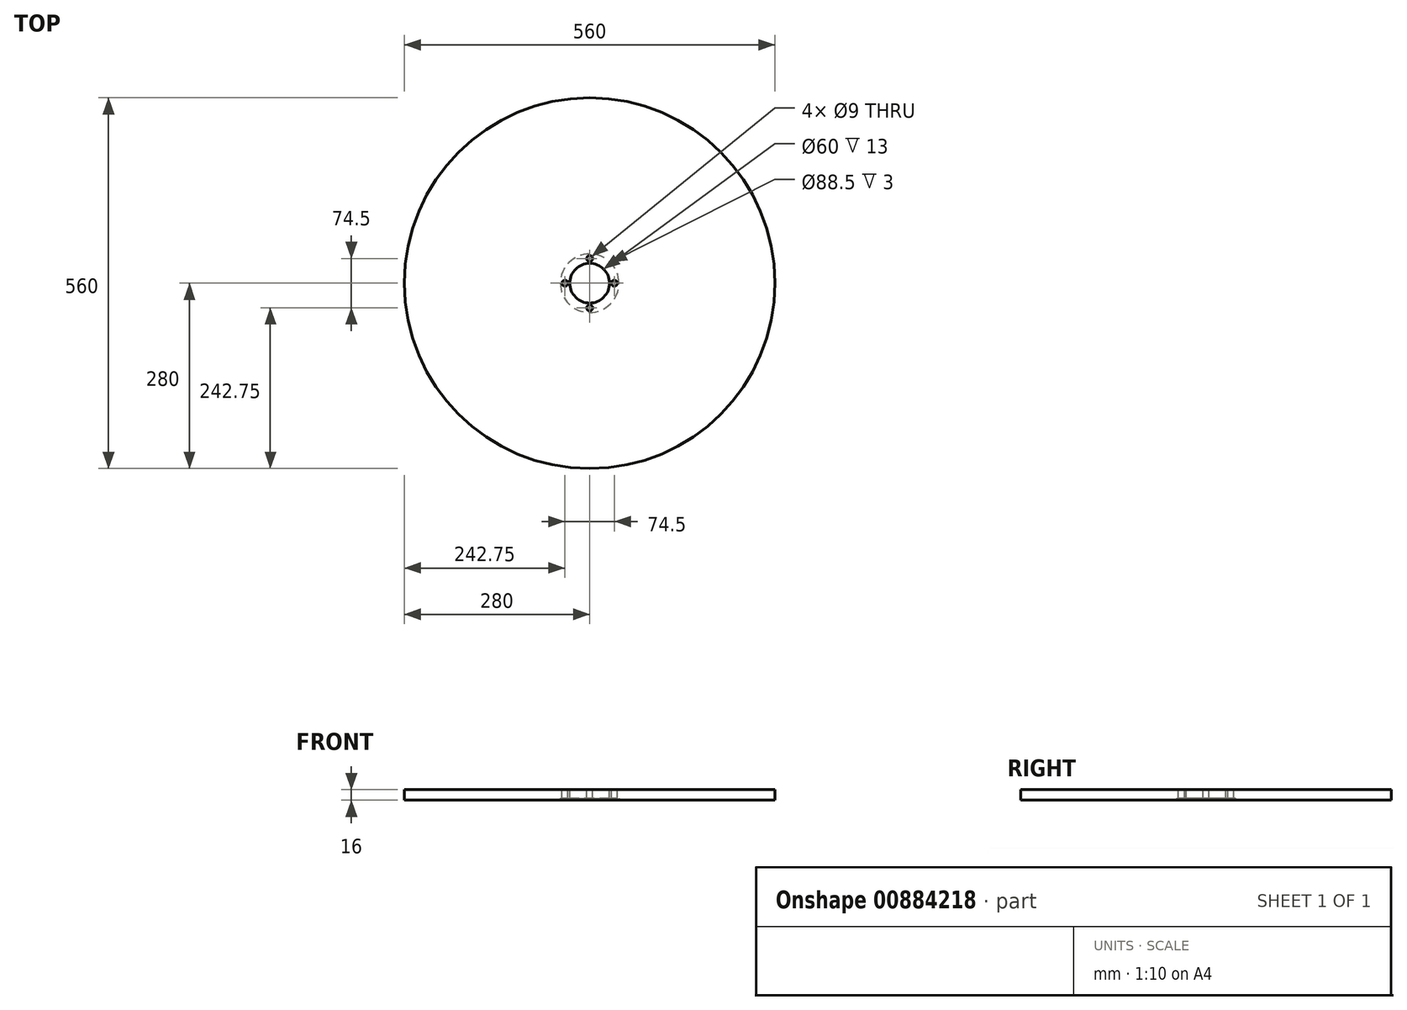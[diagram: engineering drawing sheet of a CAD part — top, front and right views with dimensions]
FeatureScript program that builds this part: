
annotation { "Feature Type Name" : "Feature", "Feature Type Description" : "" }
export const myFeature = defineFeature(function(context is Context, id is Id, definition is map)
    precondition{}
    {
        {
            var Q0;
            Q0=qCreatedBy(makeId("Top.planeOp"),FACE);
            var sketch = newSketch(context, id + "F0", { "sketchPlane" : qUnion([Q0])});
            skCircle(sketch, "E0", {"center": v(0, 0) * mm, "radius": 280 * mm});
            skSolve(sketch);
        }
        {
            var Q0;
            Q0=makeQuery(id+"F0.imprint","IMPRINT",FACE,{"disambiguationData":[TD([[makeQuery(id+"F0.imprint","IMPRINT",EDGE,{"derivedFrom":sQuery(id+"F0.wireOp",EDGE,"E0")}),1.0]])]});
            extrude(context, id + "F1", {"entities" : qUnion([Q0]), "depth" : 16 * mm, "offsetDistance" : 25 * mm});
        }
        {
            var Q0;
            Q0=makeQuery(id+"F1.opExtrude","CAP_FACE",FACE,{"disambiguationData":[OSD([sQuery(id+"F0.wireOp",EDGE,"E0")])],"isStart":false});
            var sketch = newSketch(context, id + "F2", { "sketchPlane" : qUnion([Q0])});
            skCircle(sketch, "E1", {"center": v(0, 0) * mm, "radius": 30 * mm});
            skCircle(sketch, "E2", {"center": v(0, 0) * mm, "radius": 37.25 * mm, "construction": true});
            skCircle(sketch, "E3", {"center": v(0, 37.25) * mm, "radius": 4.5 * mm});
            skCircle(sketch, "E4", {"center": v(-37.25, 0) * mm, "radius": 4.5 * mm});
            skCircle(sketch, "E5", {"center": v(37.25, 0) * mm, "radius": 4.5 * mm});
            skCircle(sketch, "E6", {"center": v(0, -37.25) * mm, "radius": 4.5 * mm});
            skSolve(sketch);
        }
        {
            var Q0;
            Q0=makeQuery(id+"F2.imprint","IMPRINT",FACE,{"disambiguationData":[TD([[makeQuery(id+"F2.imprint","IMPRINT",EDGE,{"derivedFrom":sQuery(id+"F2.wireOp",EDGE,"E1")}),1.0]])]});
            var Q1;
            Q1=makeQuery(id+"F2.imprint","IMPRINT",FACE,{"disambiguationData":[TD([[makeQuery(id+"F2.imprint","IMPRINT",EDGE,{"derivedFrom":sQuery(id+"F2.wireOp",EDGE,"HDDMHsGB-oVZA-M6vI-Bz3S-lTRq8NOSrvcb")}),1.0]])]});
            var Q2;
            Q2=makeQuery(id+"F2.imprint","IMPRINT",FACE,{"disambiguationData":[TD([[makeQuery(id+"F2.imprint","IMPRINT",EDGE,{"derivedFrom":sQuery(id+"F2.wireOp",EDGE,"E4")}),1.0]])]});
            var Q3;
            Q3=makeQuery(id+"F2.imprint","IMPRINT",FACE,{"disambiguationData":[TD([[makeQuery(id+"F2.imprint","IMPRINT",EDGE,{"derivedFrom":sQuery(id+"F2.wireOp",EDGE,"E3")}),1.0]])]});
            var Q4;
            Q4=makeQuery(id+"F2.imprint","IMPRINT",FACE,{"disambiguationData":[TD([[makeQuery(id+"F2.imprint","IMPRINT",EDGE,{"derivedFrom":sQuery(id+"F2.wireOp",EDGE,"E5")}),1.0]])]});
            var Q5;
            Q5=makeQuery(id+"F2.imprint","IMPRINT",FACE,{"disambiguationData":[TD([[makeQuery(id+"F2.imprint","IMPRINT",EDGE,{"derivedFrom":sQuery(id+"F2.wireOp",EDGE,"E6")}),1.0]])]});
            extrude(context, id + "F3", {"entities" : qUnion([Q0, Q1, Q2, Q3, Q4, Q5]), "operationType" : NewBodyOperationType.REMOVE, "oppositeDirection" : true, "depth" : 25 * mm, "offsetDistance" : 25 * mm});
        }
        {
            var Q0;
            Q0=makeQuery(id+"F1.opExtrude","CAP_FACE",FACE,{"disambiguationData":[OSD([sQuery(id+"F0.wireOp",EDGE,"E0")])],"isStart":true});
            var sketch = newSketch(context, id + "F4", { "sketchPlane" : qUnion([Q0])});
            skCircle(sketch, "E7", {"center": v(0, 0) * mm, "radius": 44.25 * mm});
            skSolve(sketch);
        }
        {
            var Q0;
            Q0=makeQuery(id+"F4.imprint","IMPRINT",FACE,{"disambiguationData":[TD([[makeQuery(id+"F4.imprint","IMPRINT",EDGE,{"derivedFrom":sQuery(id+"F4.wireOp",EDGE,"E7")}),1.0]])]});
            extrude(context, id + "F5", {"entities" : qUnion([Q0]), "operationType" : NewBodyOperationType.REMOVE, "oppositeDirection" : true, "depth" : 3 * mm, "offsetDistance" : 25 * mm});
        }
    });
